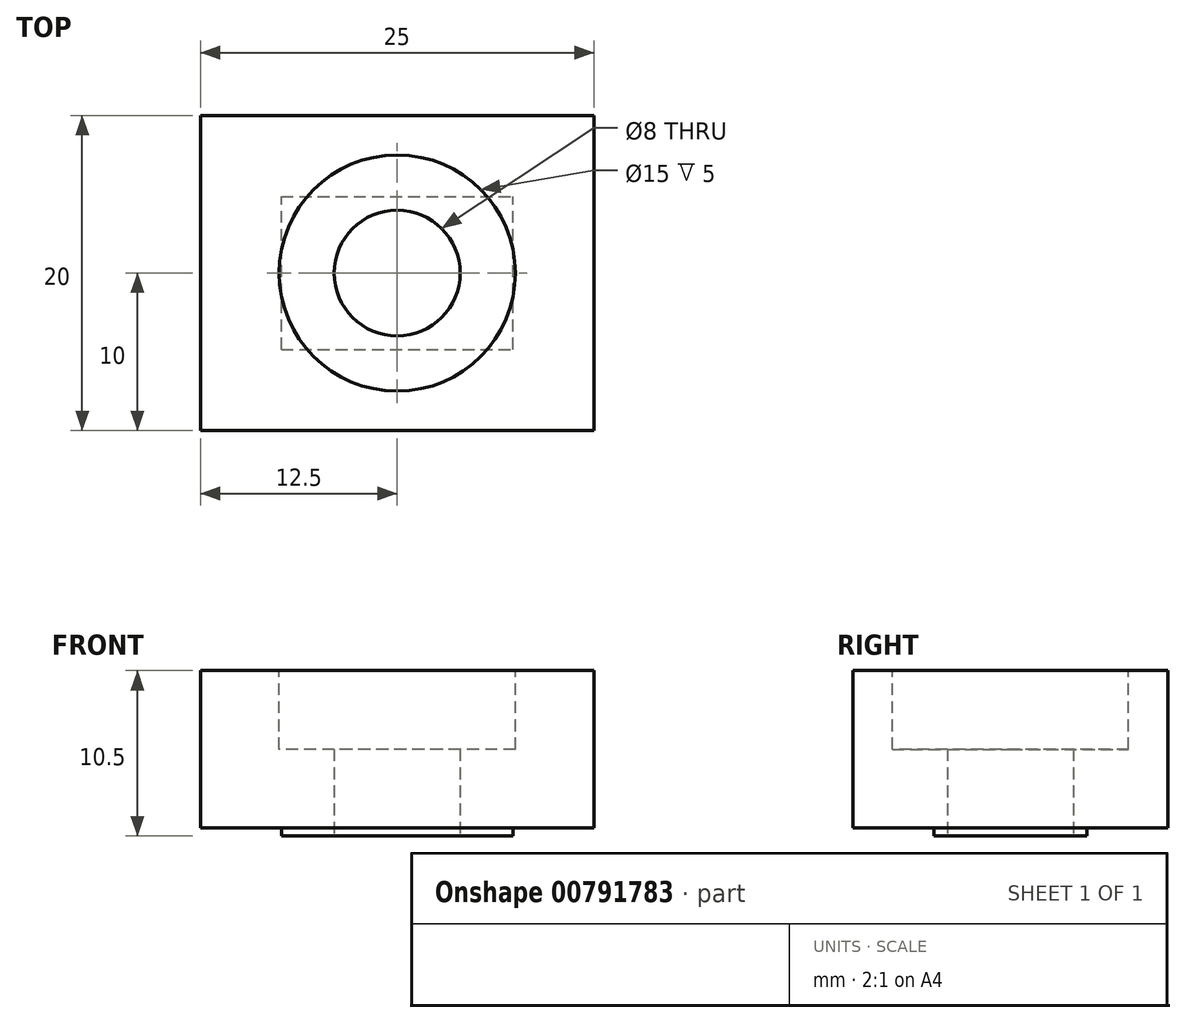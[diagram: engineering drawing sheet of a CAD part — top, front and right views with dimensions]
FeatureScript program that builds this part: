
annotation { "Feature Type Name" : "Feature", "Feature Type Description" : "" }
export const myFeature = defineFeature(function(context is Context, id is Id, definition is map)
    precondition{}
    {
        {
            var Q0;
            Q0=qCreatedBy(makeId("Top.planeOp"),FACE);
            var sketch = newSketch(context, id + "F0", { "sketchPlane" : qUnion([Q0])});
            skLineSegment(sketch, "E0.bottom", {"start": v(-12.5, 10) * mm, "end": v(12.5, 10) * mm});
            skLineSegment(sketch, "E0.top", {"start": v(-12.5, -10) * mm, "end": v(12.5, -10) * mm});
            skLineSegment(sketch, "E0.left", {"start": v(-12.5, 10) * mm, "end": v(-12.5, -10) * mm});
            skLineSegment(sketch, "E0.right", {"start": v(12.5, 10) * mm, "end": v(12.5, -10) * mm});
            skCircle(sketch, "E1", {"center": v(0, 0) * mm, "radius": 4 * mm});
            skSolve(sketch);
        }
        {
            var Q0;
            Q0=qSketchRegion(id+"F0",true);
            extrude(context, id + "F1", {"entities" : qUnion([Q0]), "depth" : 10 * mm, "offsetDistance" : 25 * mm});
        }
        {
            var Q0;
            Q0=makeQuery(id+"F1.opExtrude","CAP_FACE",FACE,{"disambiguationData":[OSD([sQuery(id+"F0.wireOp",EDGE,"E0.bottom"),sQuery(id+"F0.wireOp",EDGE,"E0.top"),sQuery(id+"F0.wireOp",EDGE,"E0.left"),sQuery(id+"F0.wireOp",EDGE,"E0.right"),sQuery(id+"F0.wireOp",EDGE,"E1")])],"isStart":false});
            var sketch = newSketch(context, id + "F2", { "sketchPlane" : qUnion([Q0])});
            skCircle(sketch, "E2", {"center": v(0, 0) * mm, "radius": 7.5 * mm});
            skSolve(sketch);
        }
        {
            var Q0;
            Q0=qSketchRegion(id+"F2",true);
            extrude(context, id + "F3", {"entities" : qUnion([Q0]), "operationType" : NewBodyOperationType.REMOVE, "oppositeDirection" : true, "depth" : 5 * mm, "offsetDistance" : 25 * mm});
        }
        {
            var Q0;
            Q0=makeQuery(id+"F1.opExtrude","CAP_FACE",FACE,{"disambiguationData":[OSD([sQuery(id+"F0.wireOp",EDGE,"E0.bottom"),sQuery(id+"F0.wireOp",EDGE,"E0.top"),sQuery(id+"F0.wireOp",EDGE,"E0.left"),sQuery(id+"F0.wireOp",EDGE,"E0.right"),sQuery(id+"F0.wireOp",EDGE,"E1")])],"isStart":true});
            var sketch = newSketch(context, id + "F4", { "sketchPlane" : qUnion([Q0])});
            skLineSegment(sketch, "E3.bottom", {"start": v(-7.35, 4.85) * mm, "end": v(7.35, 4.85) * mm});
            skLineSegment(sketch, "E3.top", {"start": v(-7.35, -4.85) * mm, "end": v(7.35, -4.85) * mm});
            skLineSegment(sketch, "E3.left", {"start": v(-7.35, 4.85) * mm, "end": v(-7.35, -4.85) * mm});
            skLineSegment(sketch, "E3.right", {"start": v(7.35, 4.85) * mm, "end": v(7.35, -4.85) * mm});
            skSolve(sketch);
        }
        {
            var Q0;
            Q0=makeQuery(id+"F4.imprint","IMPRINT",FACE,{"disambiguationData":[TD([[makeQuery(id+"F4.imprint","IMPRINT",EDGE,{"derivedFrom":sQuery(id+"F4.wireOp",EDGE,"E3.bottom")}),-1.0]])]});
            extrude(context, id + "F5", {"entities" : qUnion([Q0]), "operationType" : NewBodyOperationType.ADD, "depth" : 0.5 * mm, "offsetDistance" : 25 * mm});
        }
    });
